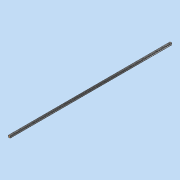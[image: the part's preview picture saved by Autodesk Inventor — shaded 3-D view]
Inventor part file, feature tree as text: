
AUTODESK INVENTOR PART (.ipt)
format: ipt  version: 2021 (Build 250183000, 183)  size: 343,040 bytes
history: native  units: mm
features: sketch x4, extrude x3, projected_geometry x3, other x2
ambient origin geometry x8: Origin, YZ Plane, XZ Plane, XY Plane, X Axis, Y Axis, Z Axis, Center Point
bodies: Solid1 (feature_tree)
feature tree (12):
  extrude  "Extrusion1"  Depth=1500.0mm
  sketch  "Sketch2"  dims[d4=6.0mm d6=9.5mm d7=6.0mm]
  extrude  "Extrusion2"  Depth=9.5mm
  extrude  "Extrusion3"  Depth=9.5mm
  sketch  "Sketch3"  dims[d9=9.5mm d10=6.0mm d12=9.5mm d13=6.0mm]
  other  "Work Axis1"
  sketch  "Sketch4"  dims[d15=9.5mm d16=6.0mm d18=9.5mm d19=6.0mm d21=9.5mm d22=6.0mm d24=9.5mm d25=6.0mm d27=9.5mm d28=6.0mm d30=9.5mm d31=6.0mm d33=9.5mm d34=6.0mm d36=9.5mm d37=6.0mm d39=9.5mm d40=6.0mm d42=9.5mm d43=6.0mm d45=9.5mm d46=6.0mm d48=9.5mm d49=6.0mm d51=9.5mm d52=6.0mm d54=9.5mm d55=6.0mm d57=9.5mm d58=6.0mm d60=9.5mm d61=6.0mm d63=9.5mm d64=6.0mm d66=9.5mm d67=6.0mm d69=9.5mm d70=6.0mm d72=9.5mm d73=6.0mm d75=9.5mm d76=6.0mm d78=30.0mm d79=0.0mm d80=8.4mm d81=0.0mm]
  other  "Work Axis2"
  sketch  "Sketch1"  dims[d0=1500.0mm d1=0.0mm d3=9.5mm]
  projected_geometry  "Projected Loop1"
  projected_geometry  "Projected Loop2"
  projected_geometry  "Projected Loop3"
